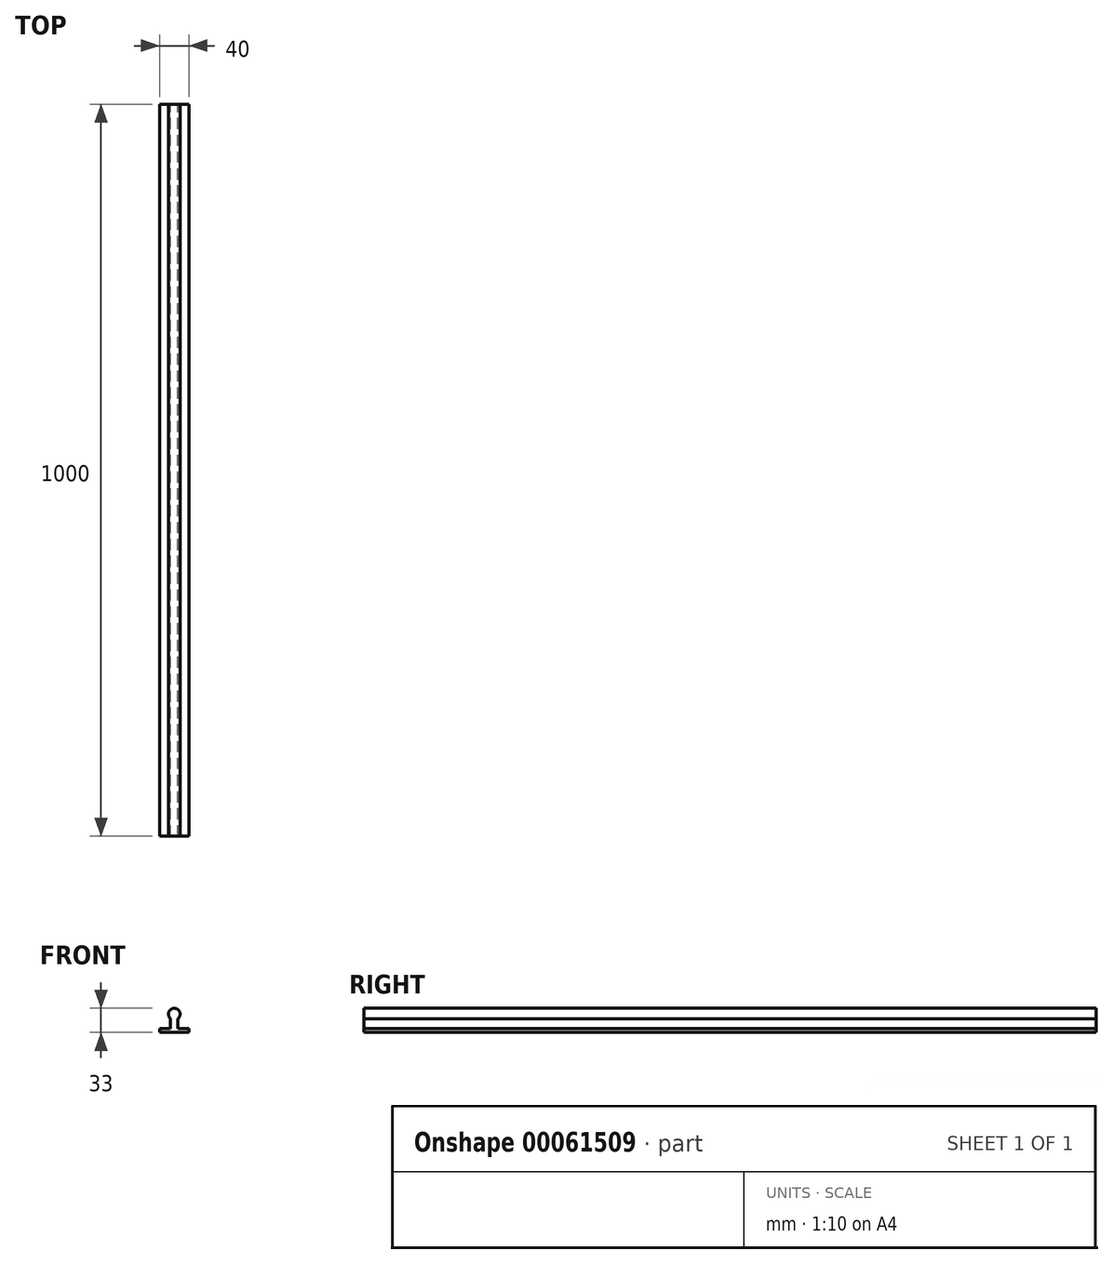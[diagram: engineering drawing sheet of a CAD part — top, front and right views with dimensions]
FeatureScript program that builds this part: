
annotation { "Feature Type Name" : "Feature", "Feature Type Description" : "" }
export const myFeature = defineFeature(function(context is Context, id is Id, definition is map)
    precondition{}
    {
        {
            var Q0;
            Q0=qCreatedBy(makeId("Front.planeOp"),FACE);
            var sketch = newSketch(context, id + "F0", { "sketchPlane" : qUnion([Q0])});
            skCircle(sketch, "E0", {"center": v(0, 0) * mm, "radius": 8 * mm});
            skLineSegment(sketch, "E1", {"start": v(5, 0) * mm, "end": v(5, -20) * mm});
            skLineSegment(sketch, "E2", {"start": v(5, -20) * mm, "end": v(-20, -20) * mm});
            skLineSegment(sketch, "E3", {"start": v(-20, -20) * mm, "end": v(-20, -25) * mm});
            skLineSegment(sketch, "E4", {"start": v(-20, -25) * mm, "end": v(0, -25) * mm});
            skLineSegment(sketch, "E5.MirrorCS", {"start": v(20, -25) * mm, "end": v(0, -25) * mm});
            skLineSegment(sketch, "E6.MirrorCS", {"start": v(20, -20) * mm, "end": v(20, -25) * mm});
            skLineSegment(sketch, "E7.MirrorCS", {"start": v(-5, -20) * mm, "end": v(20, -20) * mm});
            skLineSegment(sketch, "E8.MirrorCS", {"start": v(-5, 0) * mm, "end": v(-5, -20) * mm});
            skSolve(sketch);
        }
        {
            var Q0;
            {var subQ0=sQuery(id+"F0.wireOp",EDGE,"E0");var subQ1=makeQuery(id+"F0.imprint","INTERSECT",VERTEX,{"derivedFrom":[subQ0,sQuery(id+"F0.wireOp",EDGE,"E1")]});Q0=makeQuery(id+"F0.imprint","IMPRINT",FACE,{"disambiguationData":[TD([[makeQuery(id+"F0.imprint","IMPRINT",EDGE,{"disambiguationData":[TD([[subQ1,1.0]])],"derivedFrom":subQ0}),1.0]])]});}
            var Q1;
            {var subQ0=sQuery(id+"F0.wireOp",EDGE,"E2");Q1=makeQuery(id+"F0.imprint","IMPRINT",FACE,{"disambiguationData":[TD([[makeQuery(id+"F0.imprint","IMPRINT",EDGE,{"derivedFrom":subQ0}),1.0]])]});}
            var Q2;
            {var subQ0=sQuery(id+"F0.wireOp",EDGE,"E1");var subQ1=sQuery(id+"F0.wireOp",EDGE,"E0");var subQ2=makeQuery(id+"F0.imprint","INTERSECT",VERTEX,{"derivedFrom":[subQ1,subQ0]});Q2=makeQuery(id+"F0.imprint","IMPRINT",FACE,{"disambiguationData":[TD([[makeQuery(id+"F0.imprint","IMPRINT",EDGE,{"disambiguationData":[TD([[subQ2,1.0]])],"derivedFrom":subQ1}),-1.0]])]});}
            extrude(context, id + "F1", {"entities" : qUnion([Q0, Q1, Q2]), "depth" : 1000 * mm, "symmetric" : true});
        }
    });
